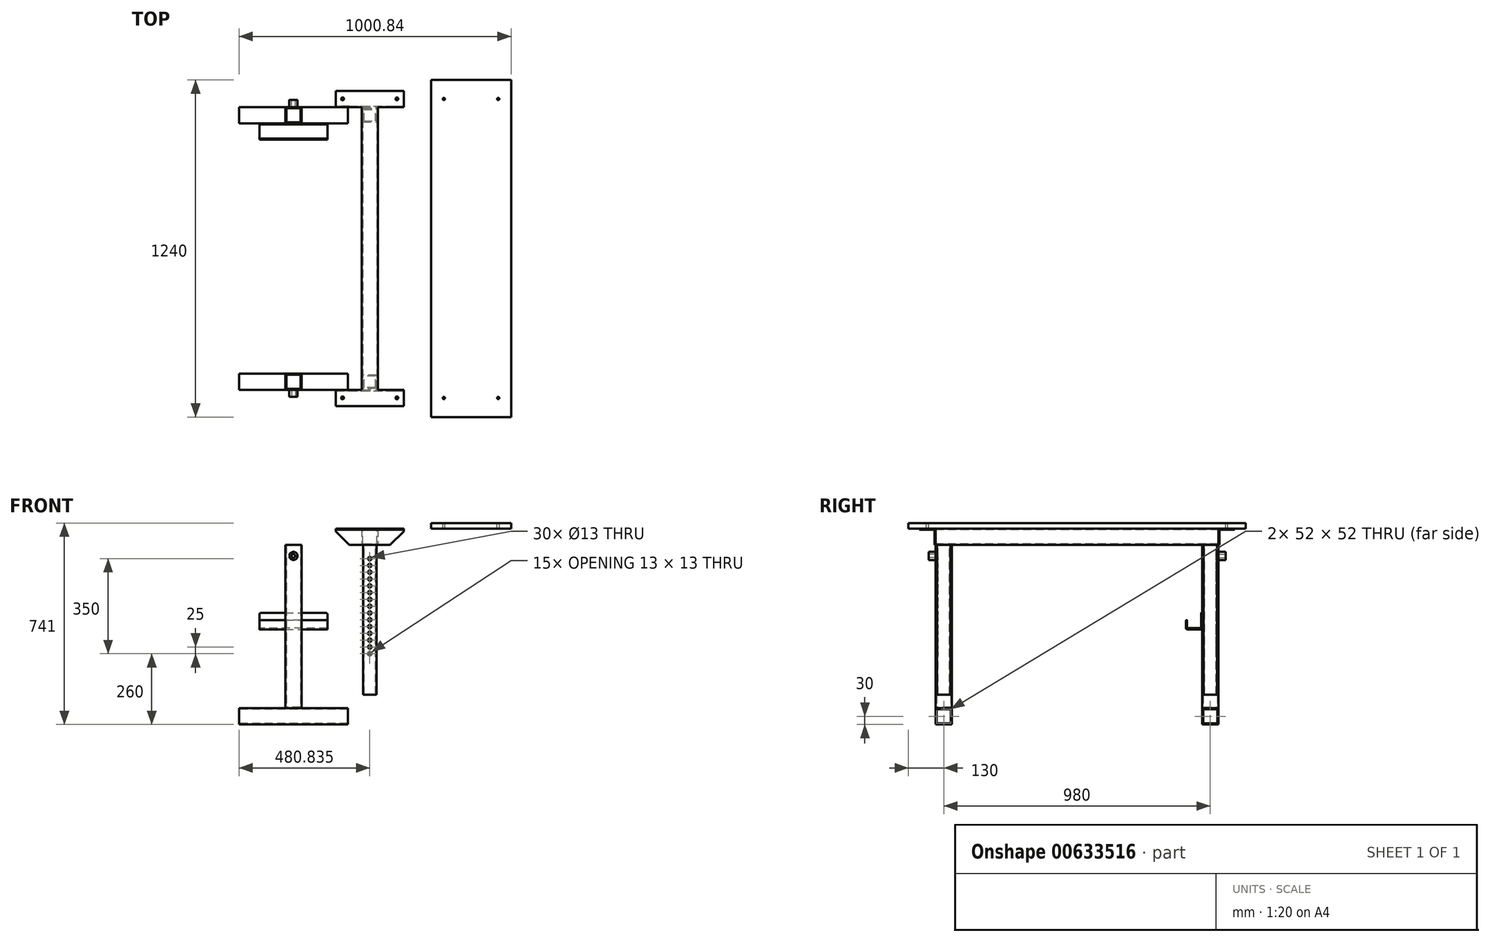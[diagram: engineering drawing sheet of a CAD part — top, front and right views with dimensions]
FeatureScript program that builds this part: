
annotation { "Feature Type Name" : "Feature", "Feature Type Description" : "" }
export const myFeature = defineFeature(function(context is Context, id is Id, definition is map)
    precondition{}
    {
        {
            var Q0;
            Q0=qCreatedBy(makeId("Top.planeOp"),FACE);
            var sketch = newSketch(context, id + "F0", { "sketchPlane" : qUnion([Q0])});
            skLineSegment(sketch, "E0.bottom", {"start": v(-200, 520) * mm, "end": v(200, 520) * mm});
            skLineSegment(sketch, "E0.top", {"start": v(-200, 460) * mm, "end": v(200, 460) * mm});
            skLineSegment(sketch, "E0.left", {"start": v(-200, 520) * mm, "end": v(-200, 460) * mm});
            skLineSegment(sketch, "E0.right", {"start": v(200, 520) * mm, "end": v(200, 460) * mm});
            skLineSegment(sketch, "E1.bottom", {"start": v(200, -460) * mm, "end": v(-200, -460) * mm});
            skLineSegment(sketch, "E1.top", {"start": v(200, -520) * mm, "end": v(-200, -520) * mm});
            skLineSegment(sketch, "E1.left", {"start": v(200, -460) * mm, "end": v(200, -520) * mm});
            skLineSegment(sketch, "E1.right", {"start": v(-200, -460) * mm, "end": v(-200, -520) * mm});
            skSolve(sketch);
        }
        {
            var Q0;
            Q0 = qSketchRegion(id + "F0", true);
            extrude(context, id + "F1", {"entities" : qUnion([Q0]), "depth" : 60 * mm, "offsetDistance" : 25 * mm});
        }
        {
            var Q0;
            Q0=makeQuery(id+"F1.opExtrude","SWEPT_FACE",FACE,{"disambiguationData":[OSD([sQuery(id+"F0.wireOp",EDGE,"E0.left")])]});
            var Q1;
            Q1=makeQuery(id+"F1.opExtrude","SWEPT_FACE",FACE,{"disambiguationData":[OSD([sQuery(id+"F0.wireOp",EDGE,"E1.right")])]});
            var Q2;
            Q2=makeQuery(id+"F1.opExtrude","SWEPT_FACE",FACE,{"disambiguationData":[OSD([sQuery(id+"F0.wireOp",EDGE,"E1.left")])]});
            var Q3;
            Q3=makeQuery(id+"F1.opExtrude","SWEPT_FACE",FACE,{"disambiguationData":[OSD([sQuery(id+"F0.wireOp",EDGE,"E0.right")])]});
            shell(context, id + "F2", {"entities" : qUnion([Q0, Q1, Q2, Q3]), "thickness" : 4 * mm});
        }
        {
            var Q0;
            Q0=makeQuery(id+"F1.opExtrude","CAP_FACE",FACE,{"disambiguationData":[OSD([sQuery(id+"F0.wireOp",EDGE,"E1.bottom"),sQuery(id+"F0.wireOp",EDGE,"E1.top"),sQuery(id+"F0.wireOp",EDGE,"E1.left"),sQuery(id+"F0.wireOp",EDGE,"E1.right")])],"isStart":false});
            var sketch = newSketch(context, id + "F3", { "sketchPlane" : qUnion([Q0])});
            skLineSegment(sketch, "E2.bottom", {"start": v(30, -460) * mm, "end": v(-30, -460) * mm});
            skLineSegment(sketch, "E2.top", {"start": v(30, -520) * mm, "end": v(-30, -520) * mm});
            skLineSegment(sketch, "E2.left", {"start": v(30, -460) * mm, "end": v(30, -520) * mm});
            skLineSegment(sketch, "E2.right", {"start": v(-30, -460) * mm, "end": v(-30, -520) * mm});
            skLineSegment(sketch, "E3.bottom", {"start": v(30, 460) * mm, "end": v(-30, 460) * mm});
            skLineSegment(sketch, "E3.top", {"start": v(30, 520) * mm, "end": v(-30, 520) * mm});
            skLineSegment(sketch, "E3.left", {"start": v(30, 460) * mm, "end": v(30, 520) * mm});
            skLineSegment(sketch, "E3.right", {"start": v(-30, 460) * mm, "end": v(-30, 520) * mm});
            skSolve(sketch);
        }
        {
            var Q0;
            Q0 = qSketchRegion(id + "F3", true);
            extrude(context, id + "F4", {"entities" : qUnion([Q0]), "depth" : 600 * mm, "offsetDistance" : 25 * mm});
        }
        {
            var Q0;
            Q0=makeQuery(id+"F4.opExtrude","CAP_FACE",FACE,{"disambiguationData":[OSD([sQuery(id+"F3.wireOp",EDGE,"E3.bottom"),sQuery(id+"F3.wireOp",EDGE,"E3.top"),sQuery(id+"F3.wireOp",EDGE,"E3.left"),sQuery(id+"F3.wireOp",EDGE,"E3.right")])],"isStart":false});
            var Q1;
            Q1=makeQuery(id+"F4.opExtrude","CAP_FACE",FACE,{"disambiguationData":[OSD([sQuery(id+"F3.wireOp",EDGE,"E2.bottom"),sQuery(id+"F3.wireOp",EDGE,"E2.top"),sQuery(id+"F3.wireOp",EDGE,"E2.left"),sQuery(id+"F3.wireOp",EDGE,"E2.right")])],"isStart":false});
            shell(context, id + "F5", {"entities" : qUnion([Q0, Q1]), "thickness" : 4 * mm});
        }
        {
            var Q0;
            Q0=makeQuery(id+"F4.opExtrude","CAP_FACE",FACE,{"disambiguationData":[OSD([sQuery(id+"F3.wireOp",EDGE,"E3.bottom"),sQuery(id+"F3.wireOp",EDGE,"E3.top"),sQuery(id+"F3.wireOp",EDGE,"E3.left"),sQuery(id+"F3.wireOp",EDGE,"E3.right")])],"isStart":false});
            var sketch = newSketch(context, id + "F6", { "sketchPlane" : qUnion([Q0])});
            skLineSegment(sketch, "E4.bottom", {"start": v(250.84, 520) * mm, "end": v(310.84, 520) * mm});
            skLineSegment(sketch, "E4.top", {"start": v(250.84, -520) * mm, "end": v(310.84, -520) * mm});
            skLineSegment(sketch, "E4.left", {"start": v(250.84, 520) * mm, "end": v(250.84, -520) * mm});
            skLineSegment(sketch, "E4.right", {"start": v(310.84, 520) * mm, "end": v(310.84, -520) * mm});
            skSolve(sketch);
        }
        {
            var Q0;
            Q0 = qSketchRegion(id + "F6", true);
            extrude(context, id + "F7", {"entities" : qUnion([Q0]), "depth" : 60 * mm, "offsetDistance" : 25 * mm});
        }
        {
            var Q0;
            Q0=makeQuery(id+"F7.opExtrude","SWEPT_FACE",FACE,{"disambiguationData":[OSD([sQuery(id+"F6.wireOp",EDGE,"E4.top")])]});
            var Q1;
            Q1=makeQuery(id+"F7.opExtrude","SWEPT_FACE",FACE,{"disambiguationData":[OSD([sQuery(id+"F6.wireOp",EDGE,"E4.bottom")])]});
            shell(context, id + "F8", {"entities" : qUnion([Q0, Q1]), "thickness" : 4 * mm});
        }
        {
            var Q0;
            Q0=makeQuery(id+"F7.opExtrude","SWEPT_FACE",FACE,{"disambiguationData":[OSD([sQuery(id+"F6.wireOp",EDGE,"E4.bottom")])]});
            var sketch = newSketch(context, id + "F9", { "sketchPlane" : qUnion([Q0])});
            skLineSegment(sketch, "E5.bottom", {"start": v(-405.84, 720) * mm, "end": v(-155.84, 720) * mm});
            skLineSegment(sketch, "E5.top", {"start": v(-405.84, 660) * mm, "end": v(-155.84, 660) * mm});
            skLineSegment(sketch, "E5.left", {"start": v(-405.84, 720) * mm, "end": v(-405.84, 660) * mm});
            skLineSegment(sketch, "E5.right", {"start": v(-155.84, 720) * mm, "end": v(-155.84, 660) * mm});
            skSolve(sketch);
        }
        {
            var Q0;
            Q0 = qSketchRegion(id + "F9", true);
            extrude(context, id + "F10", {"entities" : qUnion([Q0]), "operationType" : NewBodyOperationType.ADD, "depth" : 60 * mm, "offsetDistance" : 25 * mm});
        }
        {
            var Q0;
            Q0=makeQuery(id+"F7.opExtrude","SWEPT_FACE",FACE,{"disambiguationData":[OSD([sQuery(id+"F6.wireOp",EDGE,"E4.top")])]});
            var sketch = newSketch(context, id + "F11", { "sketchPlane" : qUnion([Q0])});
            skLineSegment(sketch, "E6.bottom", {"start": v(155.84, 720) * mm, "end": v(405.84, 720) * mm});
            skLineSegment(sketch, "E6.top", {"start": v(155.84, 660) * mm, "end": v(405.84, 660) * mm});
            skLineSegment(sketch, "E6.left", {"start": v(155.84, 720) * mm, "end": v(155.84, 660) * mm});
            skLineSegment(sketch, "E6.right", {"start": v(405.84, 720) * mm, "end": v(405.84, 660) * mm});
            skSolve(sketch);
        }
        {
            var Q0;
            Q0 = qSketchRegion(id + "F11", true);
            extrude(context, id + "F12", {"entities" : qUnion([Q0]), "operationType" : NewBodyOperationType.ADD, "depth" : 60 * mm, "offsetDistance" : 25 * mm});
        }
        {
            var Q0;
            Q0=makeQuery(id+"F12.opExtrude","SWEPT_FACE",FACE,{"disambiguationData":[OSD([sQuery(id+"F11.wireOp",EDGE,"E6.right")])]});
            var sketch = newSketch(context, id + "F13", { "sketchPlane" : qUnion([Q0])});
            skLineSegment(sketch, "E7.bottom", {"start": v(-580, 660) * mm, "end": v(-524, 660) * mm});
            skLineSegment(sketch, "E7.top", {"start": v(-580, 716) * mm, "end": v(-529, 716) * mm});
            skLineSegment(sketch, "E7.left", {"start": v(-580, 660) * mm, "end": v(-580, 716) * mm});
            skLineSegment(sketch, "E7.right", {"start": v(-524, 660) * mm, "end": v(-524, 711) * mm});
            skPoint(sketch, "E8.oppositeSnap0", {"position": v(-552, 716) * mm});
            skLineSegment(sketch, "E8.bottom", {"start": v(580, 660) * mm, "end": v(524, 660) * mm});
            skLineSegment(sketch, "E8.top", {"start": v(580, 716) * mm, "end": v(529, 716) * mm});
            skLineSegment(sketch, "E8.left", {"start": v(580, 660) * mm, "end": v(580, 716) * mm});
            skLineSegment(sketch, "E8.right", {"start": v(524, 660) * mm, "end": v(524, 711) * mm});
            skPoint(sketch, "E9.visualSharp", {"position": v(524, 716) * mm});
            skArc(sketch, "E9.filletArc", {"start": v(529, 716) * mm, "mid": v(525.46, 714.54) * mm, "end": v(524, 711) * mm});
            skPoint(sketch, "E10.visualSharp", {"position": v(-524, 716) * mm});
            skArc(sketch, "E10.filletArc", {"start": v(-524, 711) * mm, "mid": v(-525.46, 714.54) * mm, "end": v(-529, 716) * mm});
            skSolve(sketch);
        }
        {
            var Q0;
            Q0 = qSketchRegion(id + "F13", true);
            extrude(context, id + "F14", {"entities" : qUnion([Q0]), "operationType" : NewBodyOperationType.REMOVE, "oppositeDirection" : true, "depth" : 250 * mm, "offsetDistance" : 25 * mm});
        }
        {
            var Q0;
            Q0=makeQuery(id+"F12.boolean.opBoolean","MERGE",FACE,{"derivedFrom":[makeQuery(id+"F10.boolean.opBoolean","MERGE",FACE,{"derivedFrom":[makeQuery(id+"F7.opExtrude","CAP_FACE",FACE,{"disambiguationData":[OSD([sQuery(id+"F6.wireOp",EDGE,"E4.bottom"),sQuery(id+"F6.wireOp",EDGE,"E4.top"),sQuery(id+"F6.wireOp",EDGE,"E4.left"),sQuery(id+"F6.wireOp",EDGE,"E4.right")])],"isStart":false}),makeQuery(id+"F10.opExtrude","SWEPT_FACE",FACE,{"disambiguationData":[OSD([sQuery(id+"F9.wireOp",EDGE,"E5.bottom")])]})]}),makeQuery(id+"F12.opExtrude","SWEPT_FACE",FACE,{"disambiguationData":[OSD([sQuery(id+"F11.wireOp",EDGE,"E6.bottom")])]})]});
            var sketch = newSketch(context, id + "F15", { "sketchPlane" : qUnion([Q0])});
            skCircle(sketch, "E11", {"center": v(180.84, -550) * mm, "radius": 4.5 * mm});
            skCircle(sketch, "E12", {"center": v(380.84, -550) * mm, "radius": 4.5 * mm});
            skCircle(sketch, "E13", {"center": v(180.84, 550) * mm, "radius": 4.5 * mm});
            skCircle(sketch, "E14", {"center": v(380.84, 550) * mm, "radius": 4.5 * mm});
            skSolve(sketch);
        }
        {
            var Q0;
            Q0 = qSketchRegion(id + "F15", true);
            extrude(context, id + "F16", {"entities" : qUnion([Q0]), "operationType" : NewBodyOperationType.REMOVE, "oppositeDirection" : true, "depth" : 25 * mm, "offsetDistance" : 25 * mm});
        }
        {
            var Q0;
            Q0=makeQuery(id+"F16.boolean.opBoolean","INTERSECT",EDGE,{"derivedFrom":[makeQuery(id+"F14.boolean.opBoolean","COPY",FACE,{"derivedFrom":makeQuery(id+"F14.opExtrude","SWEPT_FACE",FACE,{"disambiguationData":[OSD([sQuery(id+"F13.wireOp",EDGE,"E7.top")])]})}),makeQuery(id+"F16.opExtrude","SWEPT_FACE",FACE,{"disambiguationData":[OSD([sQuery(id+"F15.wireOp",EDGE,"E11")])]})]});
            var Q1;
            Q1=makeQuery(id+"F16.boolean.opBoolean","INTERSECT",EDGE,{"derivedFrom":[makeQuery(id+"F14.boolean.opBoolean","COPY",FACE,{"derivedFrom":makeQuery(id+"F14.opExtrude","SWEPT_FACE",FACE,{"disambiguationData":[OSD([sQuery(id+"F13.wireOp",EDGE,"E7.top")])]})}),makeQuery(id+"F16.opExtrude","SWEPT_FACE",FACE,{"disambiguationData":[OSD([sQuery(id+"F15.wireOp",EDGE,"E12")])]})]});
            var Q2;
            Q2=makeQuery(id+"F16.boolean.opBoolean","INTERSECT",EDGE,{"derivedFrom":[makeQuery(id+"F14.boolean.opBoolean","COPY",FACE,{"derivedFrom":makeQuery(id+"F14.opExtrude","SWEPT_FACE",FACE,{"disambiguationData":[OSD([sQuery(id+"F13.wireOp",EDGE,"E8.top")])]})}),makeQuery(id+"F16.opExtrude","SWEPT_FACE",FACE,{"disambiguationData":[OSD([sQuery(id+"F15.wireOp",EDGE,"E14")])]})]});
            var Q3;
            Q3=makeQuery(id+"F16.boolean.opBoolean","INTERSECT",EDGE,{"derivedFrom":[makeQuery(id+"F14.boolean.opBoolean","COPY",FACE,{"derivedFrom":makeQuery(id+"F14.opExtrude","SWEPT_FACE",FACE,{"disambiguationData":[OSD([sQuery(id+"F13.wireOp",EDGE,"E8.top")])]})}),makeQuery(id+"F16.opExtrude","SWEPT_FACE",FACE,{"disambiguationData":[OSD([sQuery(id+"F15.wireOp",EDGE,"E13")])]})]});
            chamfer(context, id + "F17", {"entities" : qUnion([Q0, Q1, Q2, Q3]), "width" : 3 * mm, "tangentPropagation" : true});
        }
        {
            var Q0;
            Q0=makeQuery(id+"F12.boolean.opBoolean","MERGE",FACE,{"derivedFrom":[makeQuery(id+"F10.boolean.opBoolean","MERGE",FACE,{"derivedFrom":[makeQuery(id+"F7.opExtrude","CAP_FACE",FACE,{"disambiguationData":[OSD([sQuery(id+"F6.wireOp",EDGE,"E4.bottom"),sQuery(id+"F6.wireOp",EDGE,"E4.top"),sQuery(id+"F6.wireOp",EDGE,"E4.left"),sQuery(id+"F6.wireOp",EDGE,"E4.right")])],"isStart":true}),makeQuery(id+"F10.opExtrude","SWEPT_FACE",FACE,{"disambiguationData":[OSD([sQuery(id+"F9.wireOp",EDGE,"E5.top")])]})]}),makeQuery(id+"F12.opExtrude","SWEPT_FACE",FACE,{"disambiguationData":[OSD([sQuery(id+"F11.wireOp",EDGE,"E6.top")])]})]});
            var sketch = newSketch(context, id + "F18", { "sketchPlane" : qUnion([Q0])});
            skLineSegment(sketch, "E15.bottom", {"start": v(305.84, 515) * mm, "end": v(255.84, 515) * mm});
            skLineSegment(sketch, "E15.top", {"start": v(305.84, 465) * mm, "end": v(255.84, 465) * mm});
            skLineSegment(sketch, "E15.left", {"start": v(305.84, 515) * mm, "end": v(305.84, 465) * mm});
            skLineSegment(sketch, "E15.right", {"start": v(255.84, 515) * mm, "end": v(255.84, 465) * mm});
            skLineSegment(sketch, "E16.bottom", {"start": v(255.84, -465) * mm, "end": v(305.84, -465) * mm});
            skLineSegment(sketch, "E16.top", {"start": v(255.84, -515) * mm, "end": v(305.84, -515) * mm});
            skLineSegment(sketch, "E16.left", {"start": v(255.84, -465) * mm, "end": v(255.84, -515) * mm});
            skLineSegment(sketch, "E16.right", {"start": v(305.84, -465) * mm, "end": v(305.84, -515) * mm});
            skSolve(sketch);
        }
        {
            var Q0;
            Q0 = qSketchRegion(id + "F18", true);
            extrude(context, id + "F19", {"entities" : qUnion([Q0]), "operationType" : NewBodyOperationType.ADD, "depth" : 550 * mm, "offsetDistance" : 25 * mm});
        }
        {
            var Q0;
            Q0=makeQuery(id+"F19.opExtrude","CAP_FACE",FACE,{"disambiguationData":[OSD([sQuery(id+"F18.wireOp",EDGE,"E15.bottom"),sQuery(id+"F18.wireOp",EDGE,"E15.top"),sQuery(id+"F18.wireOp",EDGE,"E15.left"),sQuery(id+"F18.wireOp",EDGE,"E15.right")])],"isStart":false});
            var Q1;
            Q1=makeQuery(id+"F19.opExtrude","CAP_FACE",FACE,{"disambiguationData":[OSD([sQuery(id+"F18.wireOp",EDGE,"E16.bottom"),sQuery(id+"F18.wireOp",EDGE,"E16.top"),sQuery(id+"F18.wireOp",EDGE,"E16.left"),sQuery(id+"F18.wireOp",EDGE,"E16.right")])],"isStart":false});
            shell(context, id + "F20", {"entities" : qUnion([Q0, Q1]), "thickness" : 4 * mm});
        }
        {
            var Q0;
            Q0=makeQuery(id+"F4.opExtrude","SWEPT_FACE",FACE,{"disambiguationData":[OSD([sQuery(id+"F3.wireOp",EDGE,"E2.top")])]});
            var sketch = newSketch(context, id + "F21", { "sketchPlane" : qUnion([Q0])});
            skCircle(sketch, "E17", {"center": v(0, 620) * mm, "radius": 15 * mm});
            skSolve(sketch);
        }
        {
            var Q0;
            Q0 = qSketchRegion(id + "F21", true);
            extrude(context, id + "F22", {"entities" : qUnion([Q0]), "operationType" : NewBodyOperationType.ADD, "depth" : 26 * mm, "offsetDistance" : 25 * mm});
        }
        {
            var Q0;
            Q0=makeQuery(id+"F22.opExtrude","CAP_FACE",FACE,{"disambiguationData":[OSD([sQuery(id+"F21.wireOp",EDGE,"E17")])],"isStart":false});
            var sketch = newSketch(context, id + "F23", { "sketchPlane" : qUnion([Q0])});
            skCircle(sketch, "E18", {"center": v(0, 620) * mm, "radius": 6.75 * mm});
            skSolve(sketch);
        }
        {
            var Q0;
            Q0 = qSketchRegion(id + "F23", true);
            extrude(context, id + "F24", {"entities" : qUnion([Q0]), "operationType" : NewBodyOperationType.REMOVE, "oppositeDirection" : true, "depth" : 35 * mm, "offsetDistance" : 25 * mm});
        }
        {
            var Q0;
            Q0=makeQuery(id+"F4.opExtrude","SWEPT_FACE",FACE,{"disambiguationData":[OSD([sQuery(id+"F3.wireOp",EDGE,"E3.top")])]});
            var sketch = newSketch(context, id + "F25", { "sketchPlane" : qUnion([Q0])});
            skCircle(sketch, "E19", {"center": v(0, 620) * mm, "radius": 15 * mm});
            skSolve(sketch);
        }
        {
            var Q0;
            Q0 = qSketchRegion(id + "F25", true);
            extrude(context, id + "F26", {"entities" : qUnion([Q0]), "operationType" : NewBodyOperationType.ADD, "depth" : 26 * mm, "offsetDistance" : 25 * mm});
        }
        {
            var Q0;
            Q0=makeQuery(id+"F26.opExtrude","CAP_FACE",FACE,{"disambiguationData":[OSD([sQuery(id+"F25.wireOp",EDGE,"E19")])],"isStart":false});
            var sketch = newSketch(context, id + "F27", { "sketchPlane" : qUnion([Q0])});
            skCircle(sketch, "E20", {"center": v(0, 620) * mm, "radius": 6.75 * mm});
            skSolve(sketch);
        }
        {
            var Q0;
            Q0 = qSketchRegion(id + "F27", true);
            extrude(context, id + "F28", {"entities" : qUnion([Q0]), "operationType" : NewBodyOperationType.REMOVE, "oppositeDirection" : true, "depth" : 35 * mm, "offsetDistance" : 25 * mm});
        }
        {
            var Q0;
            Q0=makeQuery(id+"F19.opExtrude","SWEPT_FACE",FACE,{"disambiguationData":[OSD([sQuery(id+"F18.wireOp",EDGE,"E16.top")])]});
            var sketch = newSketch(context, id + "F29", { "sketchPlane" : qUnion([Q0])});
            skCircle(sketch, "E21", {"center": v(-280.84, 260) * mm, "radius": 6.5 * mm});
            skCircle(sketch, "E22", {"center": v(-280.84, 310) * mm, "radius": 6.5 * mm});
            skCircle(sketch, "E23", {"center": v(-280.84, 385) * mm, "radius": 6.5 * mm});
            skCircle(sketch, "E24", {"center": v(-280.84, 360) * mm, "radius": 6.5 * mm});
            skCircle(sketch, "E25", {"center": v(-280.84, 335) * mm, "radius": 6.5 * mm});
            skCircle(sketch, "E26", {"center": v(-280.84, 285) * mm, "radius": 6.5 * mm});
            skCircle(sketch, "E27", {"center": v(-280.84, 410) * mm, "radius": 6.5 * mm});
            skCircle(sketch, "E28", {"center": v(-280.84, 460) * mm, "radius": 6.5 * mm});
            skCircle(sketch, "E29", {"center": v(-280.84, 535) * mm, "radius": 6.5 * mm});
            skCircle(sketch, "E30", {"center": v(-280.84, 510) * mm, "radius": 6.5 * mm});
            skCircle(sketch, "E31", {"center": v(-280.84, 485) * mm, "radius": 6.5 * mm});
            skCircle(sketch, "E32", {"center": v(-280.84, 435) * mm, "radius": 6.5 * mm});
            skCircle(sketch, "E33", {"center": v(-280.84, 585) * mm, "radius": 6.5 * mm});
            skCircle(sketch, "E34", {"center": v(-280.84, 610) * mm, "radius": 6.5 * mm});
            skCircle(sketch, "E35", {"center": v(-280.84, 560) * mm, "radius": 6.5 * mm});
            skSolve(sketch);
        }
        {
            var Q0;
            Q0=makeQuery(id+"F19.opExtrude","SWEPT_FACE",FACE,{"disambiguationData":[OSD([sQuery(id+"F18.wireOp",EDGE,"E15.bottom")])]});
            var sketch = newSketch(context, id + "F30", { "sketchPlane" : qUnion([Q0])});
            skCircle(sketch, "E36", {"center": v(280.84, 260) * mm, "radius": 6.5 * mm});
            skCircle(sketch, "E37", {"center": v(280.84, 310) * mm, "radius": 6.5 * mm});
            skCircle(sketch, "E38", {"center": v(280.84, 385) * mm, "radius": 6.5 * mm});
            skCircle(sketch, "E39", {"center": v(280.84, 360) * mm, "radius": 6.5 * mm});
            skCircle(sketch, "E40", {"center": v(280.84, 335) * mm, "radius": 6.5 * mm});
            skCircle(sketch, "E41", {"center": v(280.84, 285) * mm, "radius": 6.5 * mm});
            skCircle(sketch, "E42", {"center": v(280.84, 410) * mm, "radius": 6.5 * mm});
            skCircle(sketch, "E43", {"center": v(280.84, 460) * mm, "radius": 6.5 * mm});
            skCircle(sketch, "E44", {"center": v(280.84, 535) * mm, "radius": 6.5 * mm});
            skCircle(sketch, "E45", {"center": v(280.84, 510) * mm, "radius": 6.5 * mm});
            skCircle(sketch, "E46", {"center": v(280.84, 485) * mm, "radius": 6.5 * mm});
            skCircle(sketch, "E47", {"center": v(280.84, 435) * mm, "radius": 6.5 * mm});
            skCircle(sketch, "E48", {"center": v(280.84, 585) * mm, "radius": 6.5 * mm});
            skCircle(sketch, "E49", {"center": v(280.84, 610) * mm, "radius": 6.5 * mm});
            skCircle(sketch, "E50", {"center": v(280.84, 560) * mm, "radius": 6.5 * mm});
            skSolve(sketch);
        }
        {
            var Q0;
            Q0 = qSketchRegion(id + "F30", true);
            extrude(context, id + "F31", {"entities" : qUnion([Q0]), "operationType" : NewBodyOperationType.REMOVE, "oppositeDirection" : true, "depth" : 25 * mm, "offsetDistance" : 25 * mm});
        }
        {
            var Q0;
            Q0 = qSketchRegion(id + "F29", true);
            extrude(context, id + "F32", {"entities" : qUnion([Q0]), "operationType" : NewBodyOperationType.REMOVE, "oppositeDirection" : true, "depth" : 25 * mm, "offsetDistance" : 25 * mm});
        }
        {
            var Q0;
            Q0=makeQuery(id+"F1.opExtrude","SWEPT_BODY",BODY,{"disambiguationData":[OSD([sQuery(id+"F0.wireOp",EDGE,"E0.bottom"),sQuery(id+"F0.wireOp",EDGE,"E0.top"),sQuery(id+"F0.wireOp",EDGE,"E0.left"),sQuery(id+"F0.wireOp",EDGE,"E0.right")])]});
            var Q1;
            Q1=makeQuery(id+"F4.opExtrude","SWEPT_BODY",BODY,{"disambiguationData":[OSD([sQuery(id+"F3.wireOp",EDGE,"E3.bottom"),sQuery(id+"F3.wireOp",EDGE,"E3.top"),sQuery(id+"F3.wireOp",EDGE,"E3.left"),sQuery(id+"F3.wireOp",EDGE,"E3.right")])]});
            booleanBodies(context, id + "F33", {"operationType" : BooleanOperationType.UNION, "tools" : qUnion([Q0, Q1])});
        }
        {
            var Q0;
            Q0=makeQuery(id+"F12.boolean.opBoolean","MERGE",FACE,{"derivedFrom":[makeQuery(id+"F10.boolean.opBoolean","MERGE",FACE,{"derivedFrom":[makeQuery(id+"F7.opExtrude","CAP_FACE",FACE,{"disambiguationData":[OSD([sQuery(id+"F6.wireOp",EDGE,"E4.bottom"),sQuery(id+"F6.wireOp",EDGE,"E4.top"),sQuery(id+"F6.wireOp",EDGE,"E4.left"),sQuery(id+"F6.wireOp",EDGE,"E4.right")])],"isStart":false}),makeQuery(id+"F10.opExtrude","SWEPT_FACE",FACE,{"disambiguationData":[OSD([sQuery(id+"F9.wireOp",EDGE,"E5.bottom")])]})]}),makeQuery(id+"F12.opExtrude","SWEPT_FACE",FACE,{"disambiguationData":[OSD([sQuery(id+"F11.wireOp",EDGE,"E6.bottom")])]})]});
            var sketch = newSketch(context, id + "F34", { "sketchPlane" : qUnion([Q0])});
            skLineSegment(sketch, "E51.bottom", {"start": v(505.84, 620) * mm, "end": v(800.84, 620) * mm});
            skLineSegment(sketch, "E51.top", {"start": v(505.84, -620) * mm, "end": v(800.84, -620) * mm});
            skLineSegment(sketch, "E51.left", {"start": v(505.84, 620) * mm, "end": v(505.84, -620) * mm});
            skLineSegment(sketch, "E51.right", {"start": v(800.84, 620) * mm, "end": v(800.84, -620) * mm});
            skSolve(sketch);
        }
        {
            var Q0;
            Q0 = qSketchRegion(id + "F34", true);
            extrude(context, id + "F35", {"entities" : qUnion([Q0]), "depth" : 21 * mm, "offsetDistance" : 25 * mm});
        }
        {
            var Q0;
            Q0=makeQuery(id+"F35.opExtrude","CAP_FACE",FACE,{"disambiguationData":[OSD([sQuery(id+"F34.wireOp",EDGE,"E51.bottom"),sQuery(id+"F34.wireOp",EDGE,"E51.top"),sQuery(id+"F34.wireOp",EDGE,"E51.left"),sQuery(id+"F34.wireOp",EDGE,"E51.right")])],"isStart":false});
            var sketch = newSketch(context, id + "F36", { "sketchPlane" : qUnion([Q0])});
            skCircle(sketch, "E52", {"center": v(553.34, 550) * mm, "radius": 4 * mm});
            skCircle(sketch, "E53", {"center": v(753.34, 550) * mm, "radius": 4 * mm});
            skCircle(sketch, "E54", {"center": v(553.34, -550) * mm, "radius": 4 * mm});
            skCircle(sketch, "E55", {"center": v(753.34, -550) * mm, "radius": 4 * mm});
            skSolve(sketch);
        }
        {
            var Q0;
            Q0 = qSketchRegion(id + "F36", true);
            extrude(context, id + "F37", {"entities" : qUnion([Q0]), "operationType" : NewBodyOperationType.REMOVE, "oppositeDirection" : true, "depth" : 25 * mm, "offsetDistance" : 25 * mm});
        }
        {
            var Q0;
            Q0=makeQuery(id+"F33.opBoolean","MERGE",FACE,{"derivedFrom":[makeQuery(id+"F1.opExtrude","SWEPT_FACE",FACE,{"disambiguationData":[OSD([sQuery(id+"F0.wireOp",EDGE,"E0.top")])]}),makeQuery(id+"F4.opExtrude","SWEPT_FACE",FACE,{"disambiguationData":[OSD([sQuery(id+"F3.wireOp",EDGE,"E3.bottom")])]})]});
            var sketch = newSketch(context, id + "F38", { "sketchPlane" : qUnion([Q0])});
            skLineSegment(sketch, "E56.bottom", {"start": v(-125, 410) * mm, "end": v(125, 410) * mm});
            skLineSegment(sketch, "E56.top", {"start": v(-125, 350) * mm, "end": v(125, 350) * mm});
            skLineSegment(sketch, "E56.left", {"start": v(-125, 410) * mm, "end": v(-125, 350) * mm});
            skLineSegment(sketch, "E56.right", {"start": v(125, 410) * mm, "end": v(125, 350) * mm});
            skSolve(sketch);
        }
        {
            var Q0;
            Q0 = qSketchRegion(id + "F38", true);
            extrude(context, id + "F39", {"entities" : qUnion([Q0]), "operationType" : NewBodyOperationType.ADD, "depth" : 60 * mm, "offsetDistance" : 25 * mm});
        }
        {
            var Q0;
            Q0=makeQuery(id+"F39.opExtrude","SWEPT_FACE",FACE,{"disambiguationData":[OSD([sQuery(id+"F38.wireOp",EDGE,"E56.left")])]});
            var sketch = newSketch(context, id + "F40", { "sketchPlane" : qUnion([Q0])});
            skLineSegment(sketch, "E57.top", {"start": v(-451, 354) * mm, "end": v(-409, 354) * mm});
            skLineSegment(sketch, "E57.left", {"start": v(-456, 410) * mm, "end": v(-456, 359) * mm});
            skLineSegment(sketch, "E57.right", {"start": v(-404, 384) * mm, "end": v(-404, 359) * mm});
            skPoint(sketch, "E58.visualSharp", {"position": v(-404, 354) * mm});
            skArc(sketch, "E58.filletArc", {"start": v(-409, 354) * mm, "mid": v(-405.46, 355.46) * mm, "end": v(-404, 359) * mm});
            skPoint(sketch, "E59.visualSharp", {"position": v(-456, 354) * mm});
            skArc(sketch, "E59.filletArc", {"start": v(-456, 359) * mm, "mid": v(-454.54, 355.46) * mm, "end": v(-451, 354) * mm});
            skLineSegment(sketch, "E60", {"start": v(-404, 384) * mm, "end": v(-302.12, 384) * mm});
            skLineSegment(sketch, "E61", {"start": v(-302.12, 384) * mm, "end": v(-302.12, 410) * mm});
            skLineSegment(sketch, "E62", {"start": v(-456, 410) * mm, "end": v(-302.12, 410) * mm});
            skSolve(sketch);
        }
        {
            var Q0;
            Q0 = qSketchRegion(id + "F40", true);
            extrude(context, id + "F41", {"entities" : qUnion([Q0]), "operationType" : NewBodyOperationType.REMOVE, "oppositeDirection" : true, "depth" : 255 * mm, "offsetDistance" : 25 * mm});
        }
        {
            var Q0;
            Q0=makeQuery(id+"F39.opExtrude","CAP_EDGE",EDGE,{"disambiguationData":[OSD([sQuery(id+"F38.wireOp",EDGE,"E56.top")])],"isStart":false});
            fillet(context, id + "F42", {"entities" : qUnion([Q0]), "radius" : 5 * mm, "tangentPropagation" : true, "allowEdgeOverflow" : false});
        }
        {
            var Q0;
            {var subQ0=sQuery(id+"F38.wireOp",EDGE,"E56.left");var subQ1=sQuery(id+"F38.wireOp",EDGE,"E56.top");var subQ2=makeQuery(id+"F39.opExtrude","CAP_FACE",FACE,{"disambiguationData":[OSD([sQuery(id+"F38.wireOp",EDGE,"E56.bottom"),subQ1,subQ0,sQuery(id+"F38.wireOp",EDGE,"E56.right")])],"isStart":true});var subQ3=makeQuery(id+"F39.opExtrude","SWEPT_FACE",FACE,{"disambiguationData":[OSD([subQ1])]});Q0=makeQuery(id+"F39.boolean.opBoolean","SPLIT",EDGE,{"disambiguationData":[topologyDisambiguationEdgeConnected([subQ2,subQ3]),TD([makeQuery(id+"F4.opExtrude","SWEPT_FACE",FACE,{"disambiguationData":[OSD([sQuery(id+"F3.wireOp",EDGE,"E3.right")])]})])],"derivedFrom":makeQuery(id+"F39.opExtrude","CAP_EDGE",EDGE,{"disambiguationData":[OSD([subQ1])],"isStart":true})});}
            fillet(context, id + "F43", {"entities" : qUnion([Q0]), "radius" : 5 * mm, "tangentPropagation" : true, "allowEdgeOverflow" : false});
        }
        {
            var Q0;
            {var subQ0=sQuery(id+"F38.wireOp",EDGE,"E56.top");var subQ1=makeQuery(id+"F39.opExtrude","SWEPT_FACE",FACE,{"disambiguationData":[OSD([subQ0])]});var subQ2=sQuery(id+"F38.wireOp",EDGE,"E56.right");var subQ3=makeQuery(id+"F39.opExtrude","CAP_FACE",FACE,{"disambiguationData":[OSD([sQuery(id+"F38.wireOp",EDGE,"E56.bottom"),subQ0,sQuery(id+"F38.wireOp",EDGE,"E56.left"),subQ2])],"isStart":true});Q0=makeQuery(id+"F39.boolean.opBoolean","SPLIT",EDGE,{"disambiguationData":[topologyDisambiguationEdgeConnected([subQ3,subQ1]),TD([makeQuery(id+"F4.opExtrude","SWEPT_FACE",FACE,{"disambiguationData":[OSD([sQuery(id+"F3.wireOp",EDGE,"E3.left")])]})])],"derivedFrom":makeQuery(id+"F39.opExtrude","CAP_EDGE",EDGE,{"disambiguationData":[OSD([subQ0])],"isStart":true})});}
            fillet(context, id + "F44", {"entities" : qUnion([Q0]), "radius" : 5 * mm, "tangentPropagation" : true, "allowEdgeOverflow" : false});
        }
        {
            var Q0;
            {var subQ0=sQuery(id+"F38.wireOp",EDGE,"E56.bottom");var subQ1=sQuery(id+"F38.wireOp",EDGE,"E56.left");Q0=makeQuery(id+"F41.boolean.opBoolean","SPLIT",EDGE,{"disambiguationData":[TD([makeQuery(id+"F41.opExtrude","SWEPT_FACE",FACE,{"disambiguationData":[OSD([sQuery(id+"F40.wireOp",EDGE,"E57.left")])]})])],"derivedFrom":makeQuery(id+"F39.opExtrude","SWEPT_EDGE",EDGE,{"disambiguationData":[OSD([subQ0,subQ1])]})});}
            var Q1;
            {var subQ0=sQuery(id+"F38.wireOp",EDGE,"E56.bottom");var subQ1=sQuery(id+"F38.wireOp",EDGE,"E56.left");Q1=makeQuery(id+"F41.boolean.opBoolean","SPLIT",EDGE,{"disambiguationData":[TD([makeQuery(id+"F41.opExtrude","SWEPT_FACE",FACE,{"disambiguationData":[OSD([sQuery(id+"F40.wireOp",EDGE,"E57.right")])]})])],"derivedFrom":makeQuery(id+"F39.opExtrude","SWEPT_EDGE",EDGE,{"disambiguationData":[OSD([subQ0,subQ1])]})});}
            var Q2;
            {var subQ0=sQuery(id+"F38.wireOp",EDGE,"E56.bottom");var subQ1=sQuery(id+"F38.wireOp",EDGE,"E56.right");Q2=makeQuery(id+"F41.boolean.opBoolean","SPLIT",EDGE,{"disambiguationData":[TD([makeQuery(id+"F41.opExtrude","SWEPT_FACE",FACE,{"disambiguationData":[OSD([sQuery(id+"F40.wireOp",EDGE,"E57.left")])]})])],"derivedFrom":makeQuery(id+"F39.opExtrude","SWEPT_EDGE",EDGE,{"disambiguationData":[OSD([subQ0,subQ1])]})});}
            var Q3;
            {var subQ0=sQuery(id+"F38.wireOp",EDGE,"E56.bottom");var subQ1=sQuery(id+"F38.wireOp",EDGE,"E56.right");Q3=makeQuery(id+"F41.boolean.opBoolean","SPLIT",EDGE,{"disambiguationData":[TD([makeQuery(id+"F41.opExtrude","SWEPT_FACE",FACE,{"disambiguationData":[OSD([sQuery(id+"F40.wireOp",EDGE,"E57.right")])]})])],"derivedFrom":makeQuery(id+"F39.opExtrude","SWEPT_EDGE",EDGE,{"disambiguationData":[OSD([subQ0,subQ1])]})});}
            fillet(context, id + "F45", {"entities" : qUnion([Q0, Q1, Q2, Q3]), "radius" : 5 * mm, "tangentPropagation" : true, "allowEdgeOverflow" : false});
        }
        {
            var Q0;
            Q0=makeQuery(id+"F41.boolean.opBoolean","COPY",EDGE,{"derivedFrom":makeQuery(id+"F41.opExtrude","CAP_EDGE",EDGE,{"disambiguationData":[OSD([sQuery(id+"F40.wireOp",EDGE,"E60")])],"isStart":true})});
            var Q1;
            Q1=makeQuery(id+"F41.boolean.opBoolean","INTERSECT",EDGE,{"derivedFrom":[makeQuery(id+"F39.opExtrude","SWEPT_FACE",FACE,{"disambiguationData":[OSD([sQuery(id+"F38.wireOp",EDGE,"E56.right")])]}),makeQuery(id+"F41.opExtrude","SWEPT_FACE",FACE,{"disambiguationData":[OSD([sQuery(id+"F40.wireOp",EDGE,"E60")])]})]});
            fillet(context, id + "F46", {"entities" : qUnion([Q0, Q1]), "radius" : 5 * mm, "tangentPropagation" : true, "allowEdgeOverflow" : false});
        }
        {
            var Q0;
            Q0=makeQuery(id+"F12.opExtrude","SWEPT_EDGE",EDGE,{"disambiguationData":[OSD([sQuery(id+"F11.wireOp",EDGE,"E6.top"),sQuery(id+"F11.wireOp",EDGE,"E6.right")])]});
            var Q1;
            Q1=makeQuery(id+"F12.opExtrude","SWEPT_EDGE",EDGE,{"disambiguationData":[OSD([sQuery(id+"F11.wireOp",EDGE,"E6.top"),sQuery(id+"F11.wireOp",EDGE,"E6.left")])]});
            var Q2;
            Q2=makeQuery(id+"F10.opExtrude","SWEPT_EDGE",EDGE,{"disambiguationData":[OSD([sQuery(id+"F9.wireOp",EDGE,"E5.top"),sQuery(id+"F9.wireOp",EDGE,"E5.left")])]});
            var Q3;
            Q3=makeQuery(id+"F10.opExtrude","SWEPT_EDGE",EDGE,{"disambiguationData":[OSD([sQuery(id+"F9.wireOp",EDGE,"E5.top"),sQuery(id+"F9.wireOp",EDGE,"E5.right")])]});
            chamfer(context, id + "F47", {"entities" : qUnion([Q0, Q1, Q2, Q3]), "width" : 50 * mm, "tangentPropagation" : true});
        }
    });
